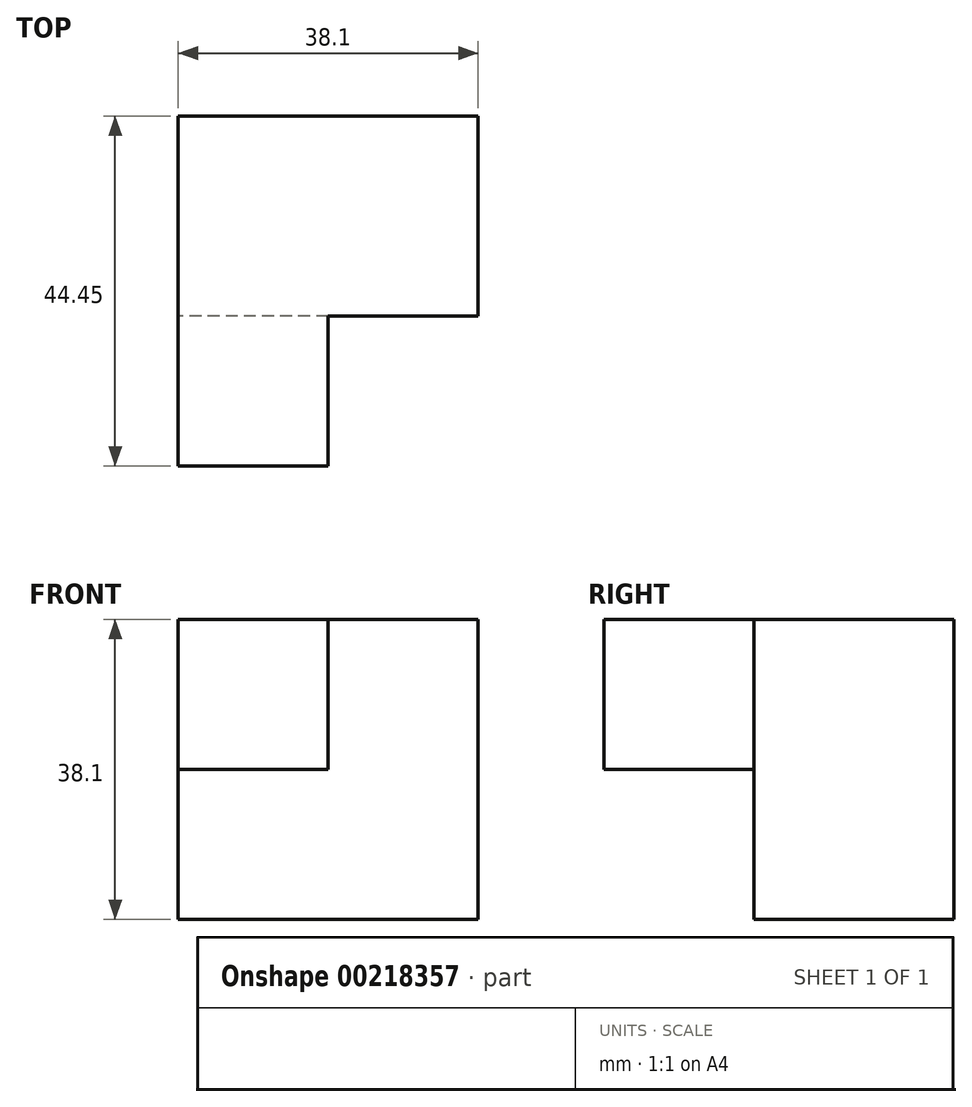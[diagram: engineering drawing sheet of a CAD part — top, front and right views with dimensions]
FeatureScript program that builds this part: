
annotation { "Feature Type Name" : "Feature", "Feature Type Description" : "" }
export const myFeature = defineFeature(function(context is Context, id is Id, definition is map)
    precondition{}
    {
        {
            var Q0;
            Q0=qCreatedBy(makeId("Front.planeOp"),FACE);
            var sketch = newSketch(context, id + "F0", { "sketchPlane" : qUnion([Q0])});
            skLineSegment(sketch, "E0.bottom", {"start": v(19.05, 19.05) * mm, "end": v(-19.05, 19.05) * mm});
            skLineSegment(sketch, "E0.top", {"start": v(19.05, -19.05) * mm, "end": v(-19.05, -19.05) * mm});
            skLineSegment(sketch, "E0.left", {"start": v(19.05, 19.05) * mm, "end": v(19.05, -19.05) * mm});
            skLineSegment(sketch, "E0.right", {"start": v(-19.05, 19.05) * mm, "end": v(-19.05, -19.05) * mm});
            skPoint(sketch, "E0.middle", {"position": v(0, 0) * mm});
            skSolve(sketch);
        }
        {
            var Q0;
            Q0=makeQuery(id+"F0.imprint","IMPRINT",FACE,{"disambiguationData":[TD([[makeQuery(id+"F0.imprint","IMPRINT",EDGE,{"derivedFrom":sQuery(id+"F0.wireOp",EDGE,"E0.bottom")}),1.0]])]});
            var sketch = newSketch(context, id + "F1", { "sketchPlane" : qUnion([Q0])});
            skLineSegment(sketch, "E1.bottom", {"start": v(-19.05, 19.05) * mm, "end": v(0, 19.05) * mm});
            skLineSegment(sketch, "E1.top", {"start": v(-19.05, 0) * mm, "end": v(0, 0) * mm});
            skLineSegment(sketch, "E1.left", {"start": v(-19.05, 19.05) * mm, "end": v(-19.05, 0) * mm});
            skLineSegment(sketch, "E1.right", {"start": v(0, 19.05) * mm, "end": v(0, 0) * mm});
            skSolve(sketch);
        }
        {
            var Q0;
            Q0 = qSketchRegion(id + "F1", true);
            extrude(context, id + "F2", {"entities" : qUnion([Q0]), "depth" : 19.05 * mm});
        }
        {
            var Q0;
            Q0=makeQuery(id+"F0.imprint","IMPRINT",FACE,{"disambiguationData":[TD([[makeQuery(id+"F0.imprint","IMPRINT",EDGE,{"derivedFrom":sQuery(id+"F0.wireOp",EDGE,"E0.bottom")}),1.0]])]});
            var Q1;
            Q1=makeQuery(id+"F2.opExtrude","CAP_FACE",FACE,{"disambiguationData":[OSD([sQuery(id+"F1.wireOp",EDGE,"E1.bottom"),sQuery(id+"F1.wireOp",EDGE,"E1.top"),sQuery(id+"F1.wireOp",EDGE,"E1.left"),sQuery(id+"F1.wireOp",EDGE,"E1.right")])],"isStart":false});
            extrude(context, id + "F3", {"entities" : qUnion([Q0, Q1]), "operationType" : NewBodyOperationType.ADD, "depth" : 25.4 * mm});
        }
    });
